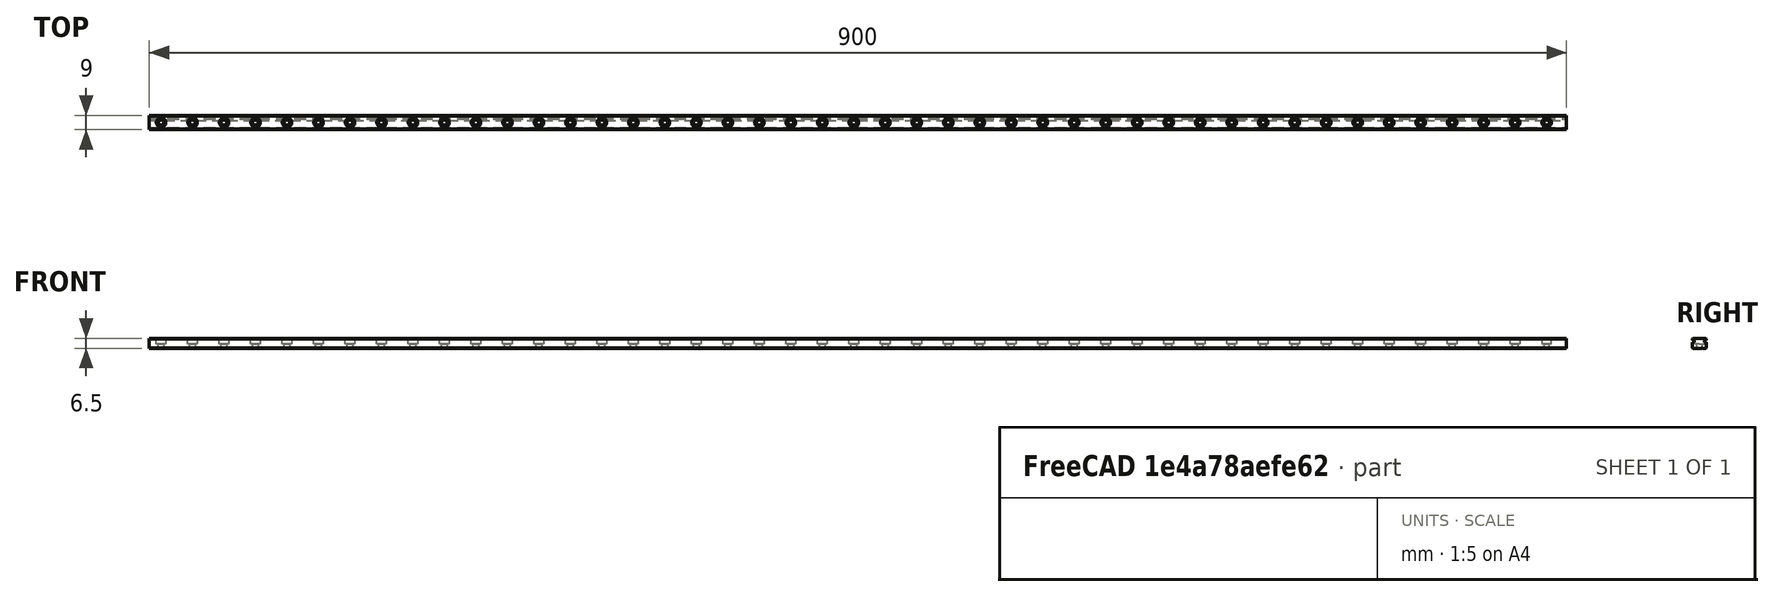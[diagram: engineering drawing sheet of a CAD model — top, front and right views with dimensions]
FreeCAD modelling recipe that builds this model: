
FCSTD DOCUMENT  (FreeCAD 2022.430R26244 +4758 (Git))
Label: as3MGNR9R900CM-HiwinCorporation-3D-10-31-2021
License: All rights reserved
LicenseURL: http://en.wikipedia.org/wiki/All_rights_reserved
objects: Part::FeaturePython×8, App::FeaturePython×2, Part::Feature×1
note: 8 computed .brp shape members not serialized (recipe doc carries the construction recipe); baked Part::Feature solids carry a one-line shape summary decoded from their .brp

FEATURE [Part::Feature] Solid  label="MGNR9R900CM-HiwinCorporation-3D-10-31-2021"
  TreeRank = 0
  shape: bbox 900 x 9 x 6.5 mm, 261 faces (baked)
FEATURE [App::FeaturePython] Constraints  # WARN: FeaturePython — macro-defined, semantics opaque (R4)
  TreeRank = 0
  _LinkVersion = 1
  _Version = 1
FEATURE [Part::FeaturePython] Parts  # WARN: FeaturePython — macro-defined, semantics opaque (R4)
  Group = -> [Solid]
  GroupMode = 0
  TreeRank = 0
  _LinkVersion = 1
FEATURE [Part::FeaturePython] Assembly  label="As3MGNR9R900CM-HiwinCorporation-3D-10-31-2021"  # WARN: FeaturePython — macro-defined, semantics opaque (R4)
  AutoRelax = true
  BuildShape = 0
  Freeze = false
  Group = -> [Constraints,Elements,Parts]
  TreeRank = 0
  Verbose = false
  _LinkVersion = 1
  _SolverType = 1
  _Version = 1
FEATURE [App::FeaturePython] Elements  # WARN: FeaturePython — macro-defined, semantics opaque (R4)
  Group = -> [Element,Element001,Element002,Element003,Element004,Element005]
  TreeRank = 0
  _LinkVersion = 1
FEATURE [Part::FeaturePython] Element  label="Extrem1"  # link proxy (typed FeaturePython)
  Detach = false
  LinkTransform = true
  LinkedObject = -> Solid [Face169]
  TreeRank = 0
  _LinkVersion = 1
  _Parent = -> Elements
FEATURE [Part::FeaturePython] Element001  label="Chanf1"  # link proxy (typed FeaturePython)
  Detach = false
  LinkTransform = true
  LinkedObject = -> Solid [Face89]
  TreeRank = 0
  _LinkVersion = 1
  _Parent = -> Elements
FEATURE [Part::FeaturePython] Element002  label="Chanf2"  # link proxy (typed FeaturePython)
  Detach = false
  LinkTransform = true
  LinkedObject = -> Solid [Face116]
  TreeRank = 0
  _LinkVersion = 1
  _Parent = -> Elements
FEATURE [Part::FeaturePython] Element003  label="Ref"  # link proxy (typed FeaturePython)
  Detach = false
  LinkTransform = true
  LinkedObject = -> Solid [Face119]
  TreeRank = 0
  _LinkVersion = 1
  _Parent = -> Elements
FEATURE [Part::FeaturePython] Element004  label="Lat"  # link proxy (typed FeaturePython)
  Detach = false
  LinkTransform = true
  LinkedObject = -> Solid [Face115]
  TreeRank = 0
  _LinkVersion = 1
  _Parent = -> Elements
FEATURE [Part::FeaturePython] Element005  label="Fix"  # link proxy (typed FeaturePython)
  Detach = false
  LinkTransform = true
  LinkedObject = -> Solid [Edge352]
  TreeRank = 0
  _LinkVersion = 1
  _Parent = -> Elements
